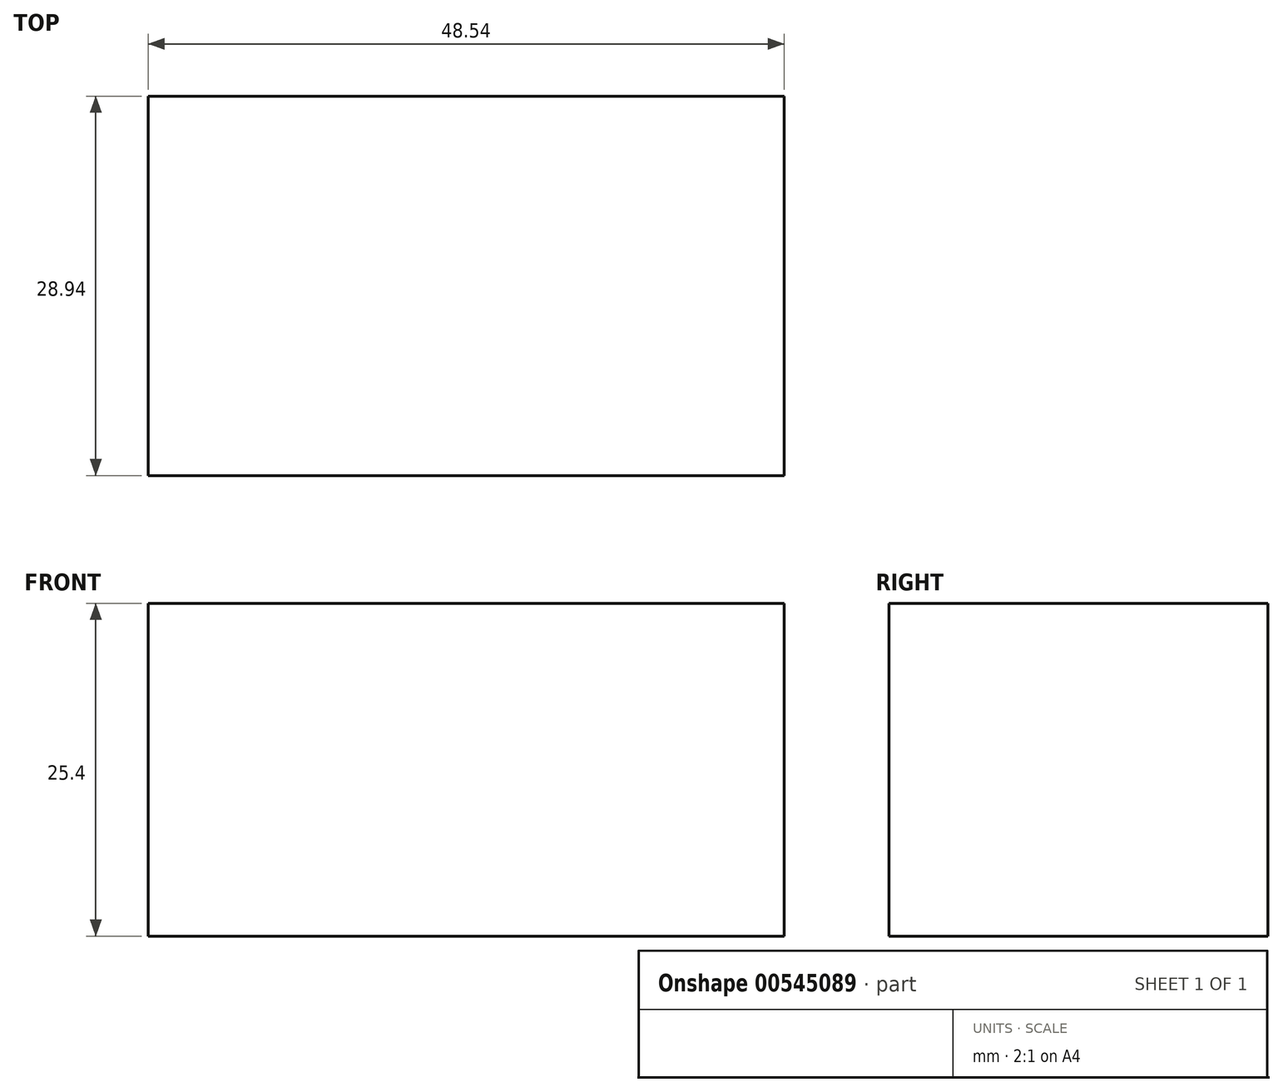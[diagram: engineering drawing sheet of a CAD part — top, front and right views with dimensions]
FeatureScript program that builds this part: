
annotation { "Feature Type Name" : "Feature", "Feature Type Description" : "" }
export const myFeature = defineFeature(function(context is Context, id is Id, definition is map)
    precondition{}
    {
        {
            var Q0;
            Q0=qCreatedBy(makeId("Top.planeOp"),FACE);
            var sketch = newSketch(context, id + "F0", { "sketchPlane" : qUnion([Q0])});
            skLineSegment(sketch, "E0.bottom", {"start": v(24.27, -14.47) * mm, "end": v(-24.27, -14.47) * mm});
            skLineSegment(sketch, "E0.top", {"start": v(24.27, 14.47) * mm, "end": v(-24.27, 14.47) * mm});
            skLineSegment(sketch, "E0.left", {"start": v(24.27, -14.47) * mm, "end": v(24.27, 14.47) * mm});
            skLineSegment(sketch, "E0.right", {"start": v(-24.27, -14.47) * mm, "end": v(-24.27, 14.47) * mm});
            skPoint(sketch, "E0.middle", {"position": v(0, 0) * mm});
            skSolve(sketch);
        }
        {
            var Q0;
            Q0=makeQuery(id+"F0.imprint","IMPRINT",FACE,{"disambiguationData":[TD([[makeQuery(id+"F0.imprint","IMPRINT",EDGE,{"derivedFrom":sQuery(id+"F0.wireOp",EDGE,"E0.bottom")}),-1.0]])]});
            extrude(context, id + "F1", {"entities" : qUnion([Q0]), "depth" : 25.4 * mm, "offsetDistance" : 25.4 * mm});
        }
    });
